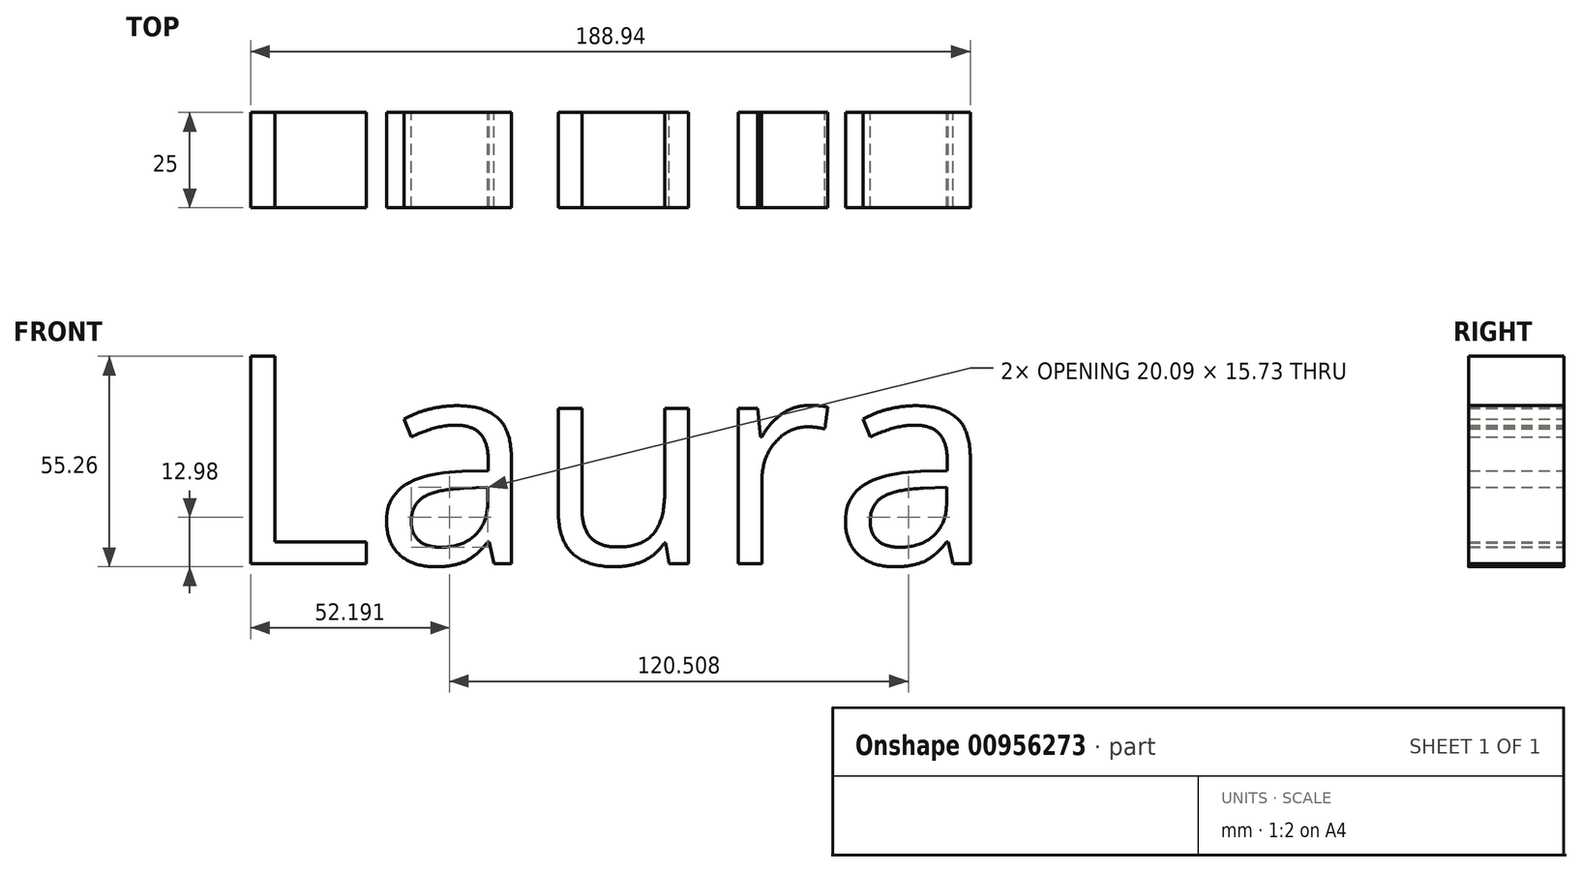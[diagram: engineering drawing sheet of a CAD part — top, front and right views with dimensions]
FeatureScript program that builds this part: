
annotation { "Feature Type Name" : "Feature", "Feature Type Description" : "" }
export const myFeature = defineFeature(function(context is Context, id is Id, definition is map)
    precondition{}
    {
        {
            var Q0;
            Q0=qCreatedBy(makeId("Front.planeOp"),FACE);
            var sketch = newSketch(context, id + "F0", { "sketchPlane" : qUnion([Q0])});
            skLineSegment(sketch, "E0.bottom", {"start": v(-100.77, 44.55) * mm, "end": v(100.77, 44.55) * mm});
            skLineSegment(sketch, "E0.top", {"start": v(-100.77, -44.55) * mm, "end": v(100.77, -44.55) * mm});
            skLineSegment(sketch, "E0.left", {"start": v(-100.77, 44.55) * mm, "end": v(-100.77, -44.55) * mm});
            skLineSegment(sketch, "E0.right", {"start": v(100.77, 44.55) * mm, "end": v(100.77, -44.55) * mm});
            skPoint(sketch, "E0.middle", {"position": v(0, 0) * mm});
            skText(sketch, "E1", { "text": "Laura", "fontName": "OpenSans-Regular.ttf"});
            const initialGuessF0  = {"E1": [-0.10077, -0.02736, 1, 0, 0.05498]};
            skSetInitialGuess(sketch, initialGuessF0);
            skSolve(sketch);
        }
        {
            var Q0;
            Q0=makeQuery(id+"F0.imprint","IMPRINT",FACE,{"disambiguationData":[TD([[makeQuery(id+"F0.imprint","IMPRINT",EDGE,{"derivedFrom":sQuery(id+"F0.wireOp",EDGE,"E1.sketch_text.stroke-0")}),-1.0]])]});
            var Q1;
            Q1=makeQuery(id+"F0.imprint","IMPRINT",FACE,{"disambiguationData":[TD([[makeQuery(id+"F0.imprint","IMPRINT",EDGE,{"derivedFrom":sQuery(id+"F0.wireOp",EDGE,"E1.sketch_text.stroke-6")}),-1.0]])]});
            var Q2;
            Q2=makeQuery(id+"F0.imprint","IMPRINT",FACE,{"disambiguationData":[TD([[makeQuery(id+"F0.imprint","IMPRINT",EDGE,{"derivedFrom":sQuery(id+"F0.wireOp",EDGE,"E1.sketch_text.stroke-33")}),-1.0]])]});
            var Q3;
            Q3=makeQuery(id+"F0.imprint","IMPRINT",FACE,{"disambiguationData":[TD([[makeQuery(id+"F0.imprint","IMPRINT",EDGE,{"derivedFrom":sQuery(id+"F0.wireOp",EDGE,"E1.sketch_text.stroke-50")}),-1.0]])]});
            var Q4;
            Q4=makeQuery(id+"F0.imprint","IMPRINT",FACE,{"disambiguationData":[TD([[makeQuery(id+"F0.imprint","IMPRINT",EDGE,{"derivedFrom":sQuery(id+"F0.wireOp",EDGE,"E1.sketch_text.stroke-63")}),-1.0]])]});
            extrude(context, id + "F1", {"entities" : qUnion([Q0, Q1, Q2, Q3, Q4]), "depth" : 25 * mm, "offsetDistance" : 25 * mm});
        }
    });
